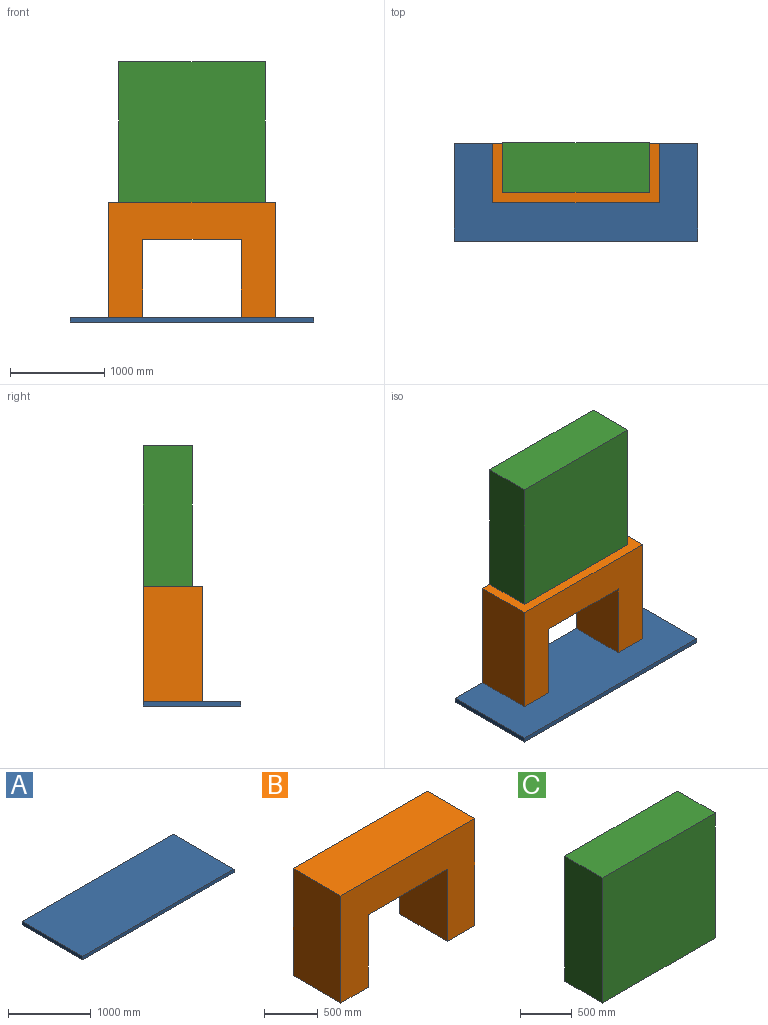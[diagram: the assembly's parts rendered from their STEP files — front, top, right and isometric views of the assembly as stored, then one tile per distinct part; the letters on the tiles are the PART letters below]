
ASSEMBLY  parts=3 mates=2
PART A: 6 faces, bbox 2578.1x1035.1x50.8 mm
  f0: plane 2578.1x50.8mm, normal (0,-1,0), area 130967.5mm2, adj f1,f3,f4,f5
  f1: plane 1035.05x50.8mm, normal (1,0,0), area 52580.5mm2, adj f0,f2,f4,f5
  f2: plane 2578.1x50.8mm, normal (0,1,0), area 130967.5mm2, adj f1,f3,f4,f5
  f3: plane 1035.05x50.8mm, normal (-1,0,0), area 52580.5mm2, adj f0,f2,f4,f5
  f4: plane 2578.1x1035.05mm, normal (0,0,1), area 2668462.4mm2, adj f0,f1,f2,f3
  f5: plane 2578.1x1035.05mm, normal (0,0,-1), area 2668462.4mm2, adj f0,f1,f2,f3
PART B: 10 faces, bbox 1765.3x628.7x1219.2 mm
  f0: plane 628.65x361.95mm, normal (0,0,-1), area 227539.9mm2, adj f2,f3,f4,f7
  f1: plane 1219.2x628.65mm, normal (-1,0,0), area 766450.1mm2, adj f2,f4,f5,f6
  f2: plane 1765.3x1219.2mm, normal (0,-1,0), area 1292578.1mm2, adj f0,f1,f3,f5,f6,f7,f8,f9
  f3: plane 1219.2x628.65mm, normal (1,0,0), area 766450.1mm2, adj f0,f2,f4,f5
  f4: plane 1765.3x1219.2mm, normal (0,1,0), area 1292578.1mm2, adj f0,f1,f3,f5,f6,f7,f8,f9
  f5: plane 1765.3x628.65mm, normal (0,0,1), area 1109755.8mm2, adj f1,f2,f3,f4
  f6: plane 628.65x361.95mm, normal (0,0,-1), area 227539.9mm2, adj f1,f2,f4,f8
  f7: plane 825.5x628.65mm, normal (-1,0,0), area 518950.6mm2, adj f0,f2,f4,f9
  f8: plane 825.5x628.65mm, normal (1,0,0), area 518950.6mm2, adj f2,f4,f6,f9
  f9: plane 1041.4x628.65mm, normal (0,0,-1), area 654676.1mm2, adj f2,f4,f7,f8
PART C: 6 faces, bbox 1549.4x520.7x1485.9 mm
  f0: plane 1485.9x520.7mm, normal (1,0,0), area 773708.1mm2, adj f1,f3,f4,f5
  f1: plane 1549.4x1485.9mm, normal (0,1,0), area 2302253.5mm2, adj f0,f2,f4,f5
  f2: plane 1485.9x520.7mm, normal (-1,0,0), area 773708.1mm2, adj f1,f3,f4,f5
  f3: plane 1549.4x1485.9mm, normal (0,-1,0), area 2302253.5mm2, adj f0,f2,f4,f5
  f4: plane 1549.4x520.7mm, normal (0,0,1), area 806772.6mm2, adj f0,f1,f2,f3
  f5: plane 1549.4x520.7mm, normal (0,0,-1), area 806772.6mm2, adj f0,f1,f2,f3
PLACE A t=(-341.4,509.79,409.72)mm
PLACE B t=(-341.4,712.99,460.52)mm
PLACE C t=(-341.4,766.97,1679.72)mm
MATE fastened B.f5 <-> C.f5  axis (0,0,1) through (-341.4,1027.32,1679.72)mm
MATE fastened A.f4 <-> B.f6  axis (0,0,1) through (-1630.45,1027.32,460.52)mm
